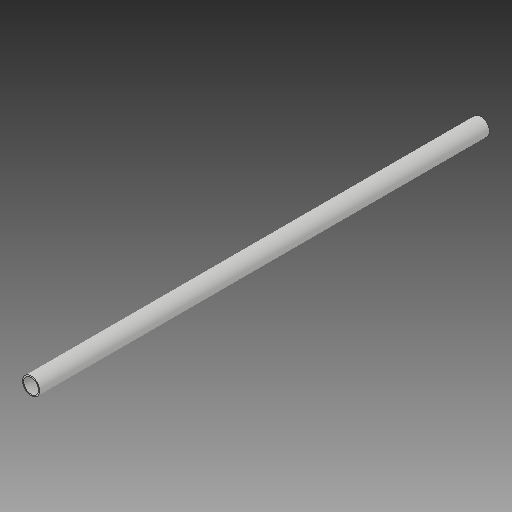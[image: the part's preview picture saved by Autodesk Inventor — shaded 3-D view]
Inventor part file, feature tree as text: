
AUTODESK INVENTOR PART (.ipt)
format: ipt  version: 2018.2 (Build 222227000, 227)  size: 92,672 bytes
history: native  units: mm
features: other x1, extrude x1, sketch x1
ambient origin geometry x8: Origin, YZ Plane, XZ Plane, XY Plane, X Axis, Y Axis, Z Axis, Center Point
bodies: Body1 (feature_tree)
feature tree (3):
  other  "ソリッド1"
  extrude  "押し出し1"  Depth=16.0mm
  sketch  "スケッチ1"
